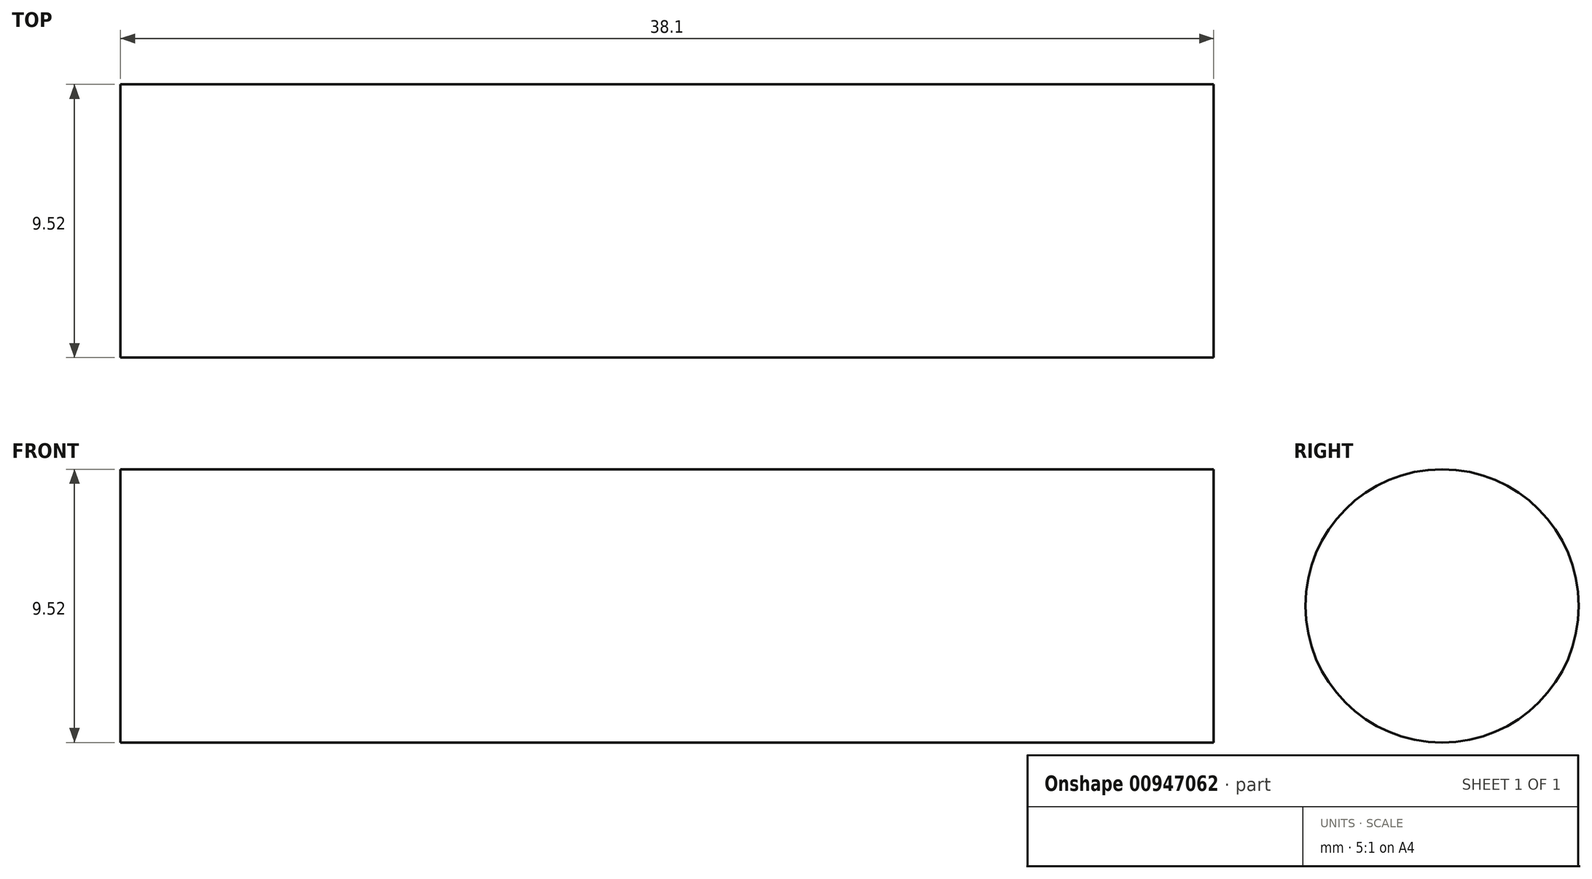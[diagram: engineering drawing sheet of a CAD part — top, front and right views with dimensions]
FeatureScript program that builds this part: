
annotation { "Feature Type Name" : "Feature", "Feature Type Description" : "" }
export const myFeature = defineFeature(function(context is Context, id is Id, definition is map)
    precondition{}
    {
        {
            var Q0;
            Q0=qCreatedBy(makeId("Right.planeOp"),FACE);
            var sketch = newSketch(context, id + "F0", { "sketchPlane" : qUnion([Q0])});
            skCircle(sketch, "E0", {"center": v(0, 0) * mm, "radius": 4.76 * mm});
            skSolve(sketch);
        }
        {
            var Q0;
            Q0=qSketchRegion(id+"F0",true);
            extrude(context, id + "F1", {"entities" : qUnion([Q0]), "endBound" : BoundingType.SYMMETRIC, "depth" : 38.1 * mm, "offsetDistance" : 25.4 * mm});
        }
    });
